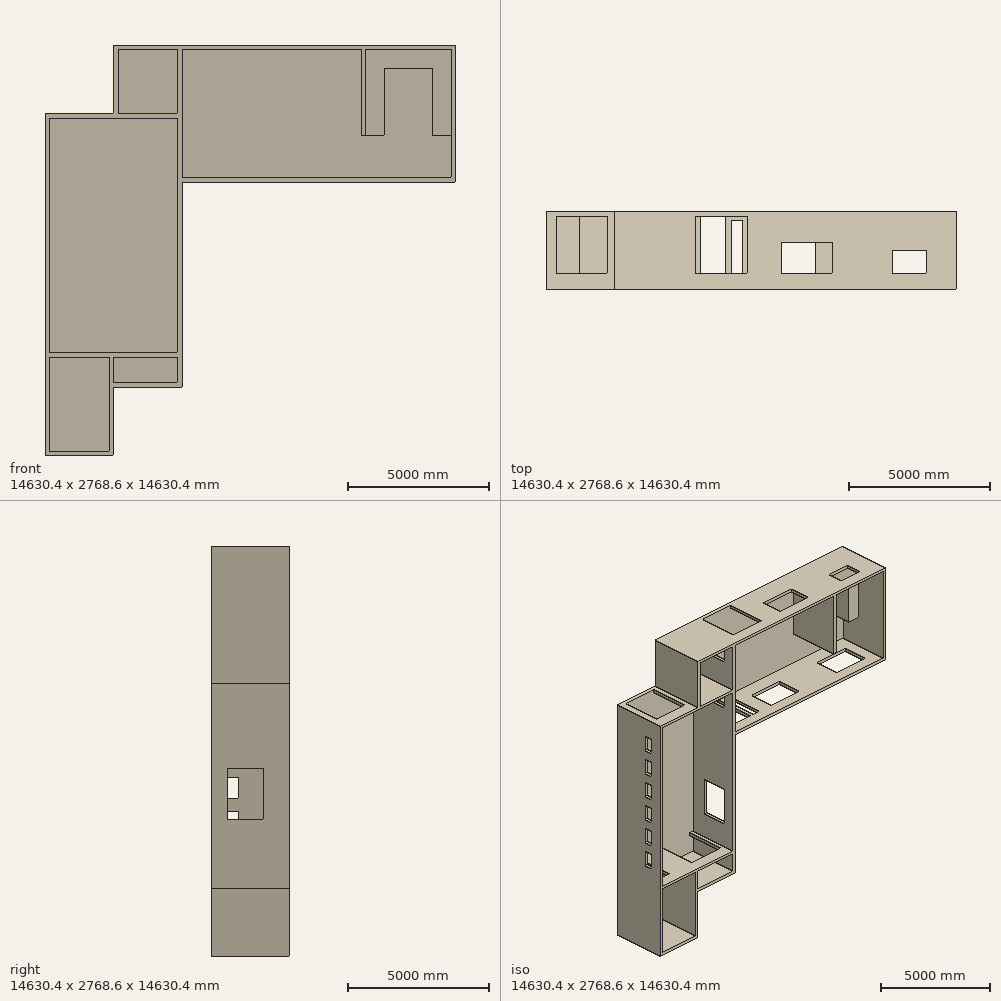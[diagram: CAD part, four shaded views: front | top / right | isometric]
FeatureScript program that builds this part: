
annotation { "Feature Type Name" : "Feature", "Feature Type Description" : "" }
export const myFeature = defineFeature(function(context is Context, id is Id, definition is map)
    precondition{}
    {
        {
            var Q0;
            Q0=qCreatedBy(makeId("Front.planeOp"),FACE);
            var sketch = newSketch(context, id + "F0", { "sketchPlane" : qUnion([Q0])});
            skLineSegment(sketch, "E0", {"start": v(0, 0) * mm, "end": v(0, 12192) * mm});
            skLineSegment(sketch, "E1", {"start": v(0, 12192) * mm, "end": v(2438.4, 12192) * mm});
            skLineSegment(sketch, "E2", {"start": v(2438.4, 12192) * mm, "end": v(2438.4, 14630.4) * mm});
            skLineSegment(sketch, "E3", {"start": v(2438.4, 14630.4) * mm, "end": v(14630.4, 14630.4) * mm});
            skLineSegment(sketch, "E4", {"start": v(14630.4, 14630.4) * mm, "end": v(14630.4, 9753.6) * mm});
            skLineSegment(sketch, "E5", {"start": v(14630.4, 9753.6) * mm, "end": v(4876.8, 9753.6) * mm});
            skLineSegment(sketch, "E6", {"start": v(4876.8, 9753.6) * mm, "end": v(4876.8, 2438.4) * mm});
            skLineSegment(sketch, "E7", {"start": v(4876.8, 2438.4) * mm, "end": v(2438.4, 2438.4) * mm});
            skLineSegment(sketch, "E8", {"start": v(2438.4, 2438.4) * mm, "end": v(2438.4, 0) * mm});
            skLineSegment(sketch, "E9", {"start": v(2438.4, 0) * mm, "end": v(0, 0) * mm});
            skLineSegment(sketch, "E10.0", {"start": v(2286, 152.4) * mm, "end": v(152.4, 152.4) * mm, "construction": true});
            skLineSegment(sketch, "E10.1", {"start": v(2286, 2590.8) * mm, "end": v(2286, 152.4) * mm, "construction": true});
            skLineSegment(sketch, "E10.2", {"start": v(152.4, 152.4) * mm, "end": v(152.4, 12039.6) * mm, "construction": true});
            skLineSegment(sketch, "E10.3", {"start": v(4724.4, 2590.8) * mm, "end": v(2286, 2590.8) * mm, "construction": true});
            skLineSegment(sketch, "E10.4", {"start": v(4724.4, 9906) * mm, "end": v(4724.4, 2590.8) * mm, "construction": true});
            skLineSegment(sketch, "E10.5", {"start": v(14478, 9906) * mm, "end": v(4724.4, 9906) * mm, "construction": true});
            skLineSegment(sketch, "E10.6", {"start": v(152.4, 12039.6) * mm, "end": v(2590.8, 12039.6) * mm, "construction": true});
            skLineSegment(sketch, "E10.7", {"start": v(2590.8, 12039.6) * mm, "end": v(2590.8, 14478) * mm, "construction": true});
            skLineSegment(sketch, "E10.8", {"start": v(2590.8, 14478) * mm, "end": v(14478, 14478) * mm, "construction": true});
            skLineSegment(sketch, "E10.9", {"start": v(14478, 14478) * mm, "end": v(14478, 9906) * mm, "construction": true});
            skSolve(sketch);
        }
        {
            var Q0;
            Q0 = qSketchRegion(id + "F0", true);
            extrude(context, id + "F1", {"entities" : qUnion([Q0]), "oppositeDirection" : true, "depth" : 177.8 * mm, "offsetDistance" : 25.4 * mm});
        }
        {
            var Q0;
            Q0=makeQuery(id+"F0.imprint","IMPRINT",FACE,{"disambiguationData":[TD([[makeQuery(id+"F0.imprint","IMPRINT",EDGE,{"derivedFrom":sQuery(id+"F0.wireOp",EDGE,"E0")}),-1.0]])]});
            var sketch = newSketch(context, id + "F2", { "sketchPlane" : qUnion([Q0])});
            skLineSegment(sketch, "E11.0", {"start": v(0, 0) * mm, "end": v(0, 12192) * mm});
            skLineSegment(sketch, "E12.0", {"start": v(0, 12192) * mm, "end": v(2438.4, 12192) * mm});
            skPoint(sketch, "E13.0", {"position": v(2438.4, 13411.2) * mm});
            skLineSegment(sketch, "E14.0", {"start": v(2438.4, 12192) * mm, "end": v(2438.4, 14630.4) * mm});
            skLineSegment(sketch, "E15.0", {"start": v(2438.4, 14630.4) * mm, "end": v(14630.4, 14630.4) * mm});
            skLineSegment(sketch, "E16.0", {"start": v(14630.4, 14630.4) * mm, "end": v(14630.4, 9753.6) * mm});
            skLineSegment(sketch, "E17.0", {"start": v(14630.4, 9753.6) * mm, "end": v(4876.8, 9753.6) * mm});
            skLineSegment(sketch, "E18.0", {"start": v(4876.8, 9753.6) * mm, "end": v(4876.8, 2438.4) * mm});
            skLineSegment(sketch, "E19.0", {"start": v(4876.8, 2438.4) * mm, "end": v(2438.4, 2438.4) * mm});
            skLineSegment(sketch, "E20.0", {"start": v(2438.4, 2438.4) * mm, "end": v(2438.4, 0) * mm});
            skLineSegment(sketch, "E21.0", {"start": v(2438.4, 0) * mm, "end": v(0, 0) * mm});
            skLineSegment(sketch, "E22.0", {"start": v(2286, 152.4) * mm, "end": v(152.4, 152.4) * mm});
            skLineSegment(sketch, "E23.0", {"start": v(2286, 2590.8) * mm, "end": v(2286, 152.4) * mm});
            skLineSegment(sketch, "E24.0", {"start": v(4724.4, 2590.8) * mm, "end": v(2286, 2590.8) * mm});
            skLineSegment(sketch, "E25.0", {"start": v(4724.4, 9906) * mm, "end": v(4724.4, 2590.8) * mm});
            skLineSegment(sketch, "E26.0", {"start": v(14478, 9906) * mm, "end": v(4724.4, 9906) * mm});
            skLineSegment(sketch, "E27.0", {"start": v(14478, 14478) * mm, "end": v(14478, 9906) * mm});
            skLineSegment(sketch, "E28.0", {"start": v(2590.8, 14478) * mm, "end": v(14478, 14478) * mm});
            skLineSegment(sketch, "E29.0", {"start": v(2590.8, 12039.6) * mm, "end": v(2590.8, 14478) * mm});
            skLineSegment(sketch, "E30.0", {"start": v(152.4, 12039.6) * mm, "end": v(2590.8, 12039.6) * mm});
            skLineSegment(sketch, "E31.0", {"start": v(152.4, 152.4) * mm, "end": v(152.4, 12039.6) * mm});
            skSolve(sketch);
        }
        {
            var Q0;
            Q0 = qSketchRegion(id + "F2", true);
            extrude(context, id + "F3", {"entities" : qUnion([Q0]), "operationType" : NewBodyOperationType.ADD, "depth" : 2590.8 * mm, "offsetDistance" : 25.4 * mm});
        }
        {
            var Q0;
            Q0=makeQuery(id+"F1.opExtrude","CAP_FACE",FACE,{"disambiguationData":[OSD([sQuery(id+"F0.wireOp",EDGE,"E0"),sQuery(id+"F0.wireOp",EDGE,"E1"),sQuery(id+"F0.wireOp",EDGE,"E2"),sQuery(id+"F0.wireOp",EDGE,"E3"),sQuery(id+"F0.wireOp",EDGE,"E4"),sQuery(id+"F0.wireOp",EDGE,"E5"),sQuery(id+"F0.wireOp",EDGE,"E6"),sQuery(id+"F0.wireOp",EDGE,"E7"),sQuery(id+"F0.wireOp",EDGE,"E8"),sQuery(id+"F0.wireOp",EDGE,"E9")])],"isStart":false});
            var sketch = newSketch(context, id + "F4", { "sketchPlane" : qUnion([Q0])});
            skLineSegment(sketch, "E32.0", {"start": v(-2235.2, 2641.6) * mm, "end": v(-2235.2, 203.2) * mm, "construction": true});
            skLineSegment(sketch, "E32.1", {"start": v(-4673.6, 2641.6) * mm, "end": v(-2235.2, 2641.6) * mm, "construction": true});
            skLineSegment(sketch, "E32.2", {"start": v(-2235.2, 203.2) * mm, "end": v(-203.2, 203.2) * mm, "construction": true});
            skLineSegment(sketch, "E32.3", {"start": v(-4673.6, 9956.8) * mm, "end": v(-4673.6, 2641.6) * mm, "construction": true});
            skLineSegment(sketch, "E32.4", {"start": v(-14427.2, 9956.8) * mm, "end": v(-4673.6, 9956.8) * mm, "construction": true});
            skLineSegment(sketch, "E32.5", {"start": v(-14427.2, 14427.2) * mm, "end": v(-14427.2, 9956.8) * mm, "construction": true});
            skLineSegment(sketch, "E32.6", {"start": v(-203.2, 203.2) * mm, "end": v(-203.2, 11988.8) * mm, "construction": true});
            skLineSegment(sketch, "E32.7", {"start": v(-203.2, 11988.8) * mm, "end": v(-2641.6, 11988.8) * mm, "construction": true});
            skLineSegment(sketch, "E32.8", {"start": v(-2641.6, 11988.8) * mm, "end": v(-2641.6, 14427.2) * mm, "construction": true});
            skLineSegment(sketch, "E32.9", {"start": v(-2641.6, 14427.2) * mm, "end": v(-14427.2, 14427.2) * mm, "construction": true});
            skCircle(sketch, "E33", {"center": v(-14427.2, 14427.2) * mm, "radius": 203.2 * mm});
            skCircle(sketch, "E34", {"center": v(-14427.2, 9956.8) * mm, "radius": 203.2 * mm});
            skCircle(sketch, "E35", {"center": v(-2641.6, 14427.2) * mm, "radius": 203.2 * mm});
            skCircle(sketch, "E36", {"center": v(-2641.6, 11988.8) * mm, "radius": 203.2 * mm});
            skCircle(sketch, "E37", {"center": v(-203.2, 11988.8) * mm, "radius": 203.2 * mm});
            skCircle(sketch, "E38", {"center": v(-203.2, 203.2) * mm, "radius": 203.2 * mm});
            skCircle(sketch, "E39", {"center": v(-2235.2, 203.2) * mm, "radius": 203.2 * mm});
            skCircle(sketch, "E40", {"center": v(-2235.2, 2641.6) * mm, "radius": 203.2 * mm});
            skCircle(sketch, "E41", {"center": v(-4673.6, 2641.6) * mm, "radius": 203.2 * mm});
            skCircle(sketch, "E42", {"center": v(-4673.6, 9956.8) * mm, "radius": 203.2 * mm});
            skLineSegment(sketch, "E43", {"start": v(-14427.2, 12192) * mm, "end": v(-2641.6, 12192) * mm, "construction": true});
            skCircle(sketch, "E44", {"center": v(-14427.2, 12192) * mm, "radius": 203.2 * mm});
            skCircle(sketch, "E45", {"center": v(-8534.4, 12192) * mm, "radius": 203.2 * mm});
            skCircle(sketch, "E46", {"center": v(-4673.6, 6299.2) * mm, "radius": 203.2 * mm});
            skCircle(sketch, "E47", {"center": v(-203.2, 6096) * mm, "radius": 203.2 * mm});
            skCircle(sketch, "E48", {"center": v(-9550.4, 9956.8) * mm, "radius": 203.2 * mm});
            skLineSegment(sketch, "E49", {"start": v(-2235.2, 2641.6) * mm, "end": v(-2235.2, 11988.8) * mm, "construction": true});
            skCircle(sketch, "E50", {"center": v(-2235.2, 7315.2) * mm, "radius": 203.2 * mm});
            skCircle(sketch, "E51", {"center": v(-8534.4, 14427.2) * mm, "radius": 203.2 * mm});
            skSolve(sketch);
        }
        {
            var Q0;
            Q0=makeQuery(id+"F1.opExtrude","CAP_FACE",FACE,{"disambiguationData":[OSD([sQuery(id+"F0.wireOp",EDGE,"E0"),sQuery(id+"F0.wireOp",EDGE,"E1"),sQuery(id+"F0.wireOp",EDGE,"E2"),sQuery(id+"F0.wireOp",EDGE,"E3"),sQuery(id+"F0.wireOp",EDGE,"E4"),sQuery(id+"F0.wireOp",EDGE,"E5"),sQuery(id+"F0.wireOp",EDGE,"E6"),sQuery(id+"F0.wireOp",EDGE,"E7"),sQuery(id+"F0.wireOp",EDGE,"E8"),sQuery(id+"F0.wireOp",EDGE,"E9")])],"isStart":true});
            var sketch = newSketch(context, id + "F5", { "sketchPlane" : qUnion([Q0])});
            skLineSegment(sketch, "E52", {"start": v(2590.8, 12039.6) * mm, "end": v(4724.4, 12039.6) * mm});
            skLineSegment(sketch, "E53", {"start": v(4724.4, 12039.6) * mm, "end": v(4724.4, 9906) * mm});
            skLineSegment(sketch, "E54.0", {"start": v(4876.8, 12192) * mm, "end": v(4876.8, 9906) * mm});
            skLineSegment(sketch, "E54.1", {"start": v(2590.8, 12192) * mm, "end": v(4876.8, 12192) * mm});
            skSolve(sketch);
        }
        {
            var Q0;
            Q0 = qSketchRegion(id + "F5", true);
            var Q1;
            {var subQ4=sQuery(id+"F5.wireOp",EDGE,"E52");Q1=makeQuery(id+"F5.imprint","IMPRINT",FACE,{"disambiguationData":[TD([[makeQuery(id+"F5.imprint","IMPRINT",EDGE,{"derivedFrom":subQ4}),1.0]])]});}
            extrude(context, id + "F6", {"entities" : qUnion([Q0, Q1]), "operationType" : NewBodyOperationType.ADD, "depth" : 2590.8 * mm, "offsetDistance" : 25.4 * mm});
        }
        {
            var Q0;
            Q0=makeQuery(id+"F3.boolean.opBoolean","MERGE",FACE,{"derivedFrom":[makeQuery(id+"F1.opExtrude","SWEPT_FACE",FACE,{"disambiguationData":[OSD([sQuery(id+"F0.wireOp",EDGE,"E5")])]}),makeQuery(id+"F3.opExtrude","SWEPT_FACE",FACE,{"disambiguationData":[OSD([sQuery(id+"F2.wireOp",EDGE,"E17.0")])]})]});
            var sketch = newSketch(context, id + "F7", { "sketchPlane" : qUnion([Q0])});
            skLineSegment(sketch, "E55.bottom", {"start": v(5486.4, 0) * mm, "end": v(6400.8, 0) * mm});
            skLineSegment(sketch, "E55.top", {"start": v(5486.4, 2032) * mm, "end": v(6400.8, 2032) * mm});
            skLineSegment(sketch, "E55.left", {"start": v(5486.4, 0) * mm, "end": v(5486.4, 2032) * mm});
            skLineSegment(sketch, "E55.right", {"start": v(6400.8, 0) * mm, "end": v(6400.8, 2032) * mm});
            skLineSegment(sketch, "E56.bottom", {"start": v(6604, 2032) * mm, "end": v(7010.4, 2032) * mm});
            skLineSegment(sketch, "E56.top", {"start": v(6604, 152.4) * mm, "end": v(7010.4, 152.4) * mm});
            skLineSegment(sketch, "E56.left", {"start": v(6604, 2032) * mm, "end": v(6604, 152.4) * mm});
            skLineSegment(sketch, "E56.right", {"start": v(7010.4, 2032) * mm, "end": v(7010.4, 152.4) * mm});
            skLineSegment(sketch, "E57.bottom", {"start": v(7772.4, 2032) * mm, "end": v(9601.2, 2032) * mm});
            skLineSegment(sketch, "E57.top", {"start": v(7772.4, 736.6) * mm, "end": v(9601.2, 736.6) * mm});
            skLineSegment(sketch, "E57.left", {"start": v(7772.4, 2032) * mm, "end": v(7772.4, 736.6) * mm});
            skLineSegment(sketch, "E57.right", {"start": v(9601.2, 2032) * mm, "end": v(9601.2, 736.6) * mm});
            skLineSegment(sketch, "E58.bottom", {"start": v(12039.6, 2032) * mm, "end": v(13868.4, 2032) * mm});
            skLineSegment(sketch, "E58.top", {"start": v(12039.6, 736.6) * mm, "end": v(13868.4, 736.6) * mm});
            skLineSegment(sketch, "E58.left", {"start": v(12039.6, 2032) * mm, "end": v(12039.6, 736.6) * mm});
            skLineSegment(sketch, "E58.right", {"start": v(13868.4, 2032) * mm, "end": v(13868.4, 736.6) * mm});
            skSolve(sketch);
        }
        {
            var Q0;
            Q0 = qSketchRegion(id + "F7", true);
            extrude(context, id + "F8", {"entities" : qUnion([Q0]), "operationType" : NewBodyOperationType.REMOVE, "endBound" : BoundingType.UP_TO_NEXT, "oppositeDirection" : true, "depth" : 25.4 * mm, "offsetDistance" : 25.4 * mm});
        }
        {
            var Q0;
            Q0=makeQuery(id+"F8.boolean.opBoolean","MERGE",FACE,{"derivedFrom":[makeQuery(id+"F6.boolean.opBoolean","SPLIT",FACE,{"disambiguationData":[TD([makeQuery(id+"F3.opExtrude","SWEPT_FACE",FACE,{"disambiguationData":[OSD([sQuery(id+"F2.wireOp",EDGE,"E26.0")])]})])],"derivedFrom":makeQuery(id+"F1.opExtrude","CAP_FACE",FACE,{"disambiguationData":[OSD([sQuery(id+"F0.wireOp",EDGE,"E0"),sQuery(id+"F0.wireOp",EDGE,"E1"),sQuery(id+"F0.wireOp",EDGE,"E2"),sQuery(id+"F0.wireOp",EDGE,"E3"),sQuery(id+"F0.wireOp",EDGE,"E4"),sQuery(id+"F0.wireOp",EDGE,"E5"),sQuery(id+"F0.wireOp",EDGE,"E6"),sQuery(id+"F0.wireOp",EDGE,"E7"),sQuery(id+"F0.wireOp",EDGE,"E8"),sQuery(id+"F0.wireOp",EDGE,"E9")])],"isStart":true})}),makeQuery(id+"F8.opExtrude","SWEPT_FACE",FACE,{"disambiguationData":[OSD([sQuery(id+"F7.wireOp",EDGE,"E55.bottom")])]})]});
            var sketch = newSketch(context, id + "F9", { "sketchPlane" : qUnion([Q0])});
            skLineSegment(sketch, "E59.bottom", {"start": v(11277.6, 14478) * mm, "end": v(11430, 14478) * mm});
            skLineSegment(sketch, "E59.top", {"start": v(11277.6, 11430) * mm, "end": v(11430, 11430) * mm});
            skLineSegment(sketch, "E59.left", {"start": v(11277.6, 14478) * mm, "end": v(11277.6, 11430) * mm});
            skLineSegment(sketch, "E59.right", {"start": v(11430, 14478) * mm, "end": v(11430, 11430) * mm});
            skSolve(sketch);
        }
        {
            var Q0;
            Q0 = qSketchRegion(id + "F9", true);
            extrude(context, id + "F10", {"entities" : qUnion([Q0]), "operationType" : NewBodyOperationType.ADD, "depth" : 2590.8 * mm, "offsetDistance" : 25.4 * mm});
        }
        {
            var Q0;
            Q0=makeQuery(id+"F6.boolean.opBoolean","SPLIT",FACE,{"disambiguationData":[TD([makeQuery(id+"F3.opExtrude","SWEPT_FACE",FACE,{"disambiguationData":[OSD([sQuery(id+"F2.wireOp",EDGE,"E22.0")])]})])],"derivedFrom":makeQuery(id+"F1.opExtrude","CAP_FACE",FACE,{"disambiguationData":[OSD([sQuery(id+"F0.wireOp",EDGE,"E0"),sQuery(id+"F0.wireOp",EDGE,"E1"),sQuery(id+"F0.wireOp",EDGE,"E2"),sQuery(id+"F0.wireOp",EDGE,"E3"),sQuery(id+"F0.wireOp",EDGE,"E4"),sQuery(id+"F0.wireOp",EDGE,"E5"),sQuery(id+"F0.wireOp",EDGE,"E6"),sQuery(id+"F0.wireOp",EDGE,"E7"),sQuery(id+"F0.wireOp",EDGE,"E8"),sQuery(id+"F0.wireOp",EDGE,"E9")])],"isStart":true})});
            var sketch = newSketch(context, id + "F11", { "sketchPlane" : qUnion([Q0])});
            skLineSegment(sketch, "E60", {"start": v(152.4, 3657.6) * mm, "end": v(4724.4, 3657.6) * mm});
            skLineSegment(sketch, "E61", {"start": v(152.4, 3505.2) * mm, "end": v(2286, 3505.2) * mm});
            skLineSegment(sketch, "E62", {"start": v(2286, 3505.2) * mm, "end": v(2286, 2590.8) * mm});
            skLineSegment(sketch, "E63", {"start": v(2438.4, 2590.8) * mm, "end": v(2438.4, 3505.2) * mm});
            skLineSegment(sketch, "E64", {"start": v(2438.4, 3505.2) * mm, "end": v(4724.4, 3505.2) * mm});
            skSolve(sketch);
        }
        {
            var Q0;
            Q0 = qSketchRegion(id + "F11", true);
            var Q1;
            {var subQ3=sQuery(id+"F11.wireOp",EDGE,"E60");Q1=makeQuery(id+"F11.imprint","IMPRINT",FACE,{"disambiguationData":[TD([[makeQuery(id+"F11.imprint","IMPRINT",EDGE,{"derivedFrom":subQ3}),-1.0]])]});}
            extrude(context, id + "F12", {"entities" : qUnion([Q0, Q1]), "operationType" : NewBodyOperationType.ADD, "depth" : 2590.8 * mm, "offsetDistance" : 25.4 * mm});
        }
        {
            var Q0;
            Q0=makeQuery(id+"F12.opExtrude","SWEPT_FACE",FACE,{"disambiguationData":[OSD([sQuery(id+"F11.wireOp",EDGE,"E60")])]});
            var sketch = newSketch(context, id + "F13", { "sketchPlane" : qUnion([Q0])});
            skLineSegment(sketch, "E65.bottom", {"start": v(355.6, 0) * mm, "end": v(1168.4, 0) * mm});
            skLineSegment(sketch, "E65.top", {"start": v(355.6, -2032) * mm, "end": v(1168.4, -2032) * mm});
            skLineSegment(sketch, "E65.left", {"start": v(355.6, 0) * mm, "end": v(355.6, -2032) * mm});
            skLineSegment(sketch, "E65.right", {"start": v(1168.4, 0) * mm, "end": v(1168.4, -2032) * mm});
            skLineSegment(sketch, "E66.bottom", {"start": v(4521.2, 0) * mm, "end": v(2641.6, 0) * mm});
            skLineSegment(sketch, "E66.top", {"start": v(4521.2, -2032) * mm, "end": v(2641.6, -2032) * mm});
            skLineSegment(sketch, "E66.left", {"start": v(4521.2, 0) * mm, "end": v(4521.2, -2032) * mm});
            skLineSegment(sketch, "E66.right", {"start": v(2641.6, 0) * mm, "end": v(2641.6, -2032) * mm});
            skSolve(sketch);
        }
        {
            var Q0;
            Q0 = qSketchRegion(id + "F13", true);
            extrude(context, id + "F14", {"entities" : qUnion([Q0]), "operationType" : NewBodyOperationType.REMOVE, "endBound" : BoundingType.UP_TO_NEXT, "oppositeDirection" : true, "depth" : 25.4 * mm, "offsetDistance" : 25.4 * mm});
        }
        {
            var Q0;
            Q0=makeQuery(id+"F8.boolean.opBoolean","MERGE",FACE,{"derivedFrom":[makeQuery(id+"F6.boolean.opBoolean","SPLIT",FACE,{"disambiguationData":[TD([makeQuery(id+"F3.opExtrude","SWEPT_FACE",FACE,{"disambiguationData":[OSD([sQuery(id+"F2.wireOp",EDGE,"E26.0")])]})])],"derivedFrom":makeQuery(id+"F1.opExtrude","CAP_FACE",FACE,{"disambiguationData":[OSD([sQuery(id+"F0.wireOp",EDGE,"E0"),sQuery(id+"F0.wireOp",EDGE,"E1"),sQuery(id+"F0.wireOp",EDGE,"E2"),sQuery(id+"F0.wireOp",EDGE,"E3"),sQuery(id+"F0.wireOp",EDGE,"E4"),sQuery(id+"F0.wireOp",EDGE,"E5"),sQuery(id+"F0.wireOp",EDGE,"E6"),sQuery(id+"F0.wireOp",EDGE,"E7"),sQuery(id+"F0.wireOp",EDGE,"E8"),sQuery(id+"F0.wireOp",EDGE,"E9")])],"isStart":true})}),makeQuery(id+"F8.opExtrude","SWEPT_FACE",FACE,{"disambiguationData":[OSD([sQuery(id+"F7.wireOp",EDGE,"E55.bottom")])]})]});
            var sketch = newSketch(context, id + "F15", { "sketchPlane" : qUnion([Q0])});
            skLineSegment(sketch, "E67", {"start": v(4876.8, 12192) * mm, "end": v(4876.8, 14478) * mm});
            skLineSegment(sketch, "E68", {"start": v(4724.4, 14478) * mm, "end": v(4724.4, 12192) * mm});
            skSolve(sketch);
        }
        {
            var Q0;
            Q0 = qSketchRegion(id + "F15", true);
            var Q1;
            {var subQ0=sQuery(id+"F15.wireOp",EDGE,"E67");Q1=makeQuery(id+"F15.imprint","IMPRINT",FACE,{"disambiguationData":[TD([[makeQuery(id+"F15.imprint","IMPRINT",EDGE,{"derivedFrom":subQ0}),1.0]])]});}
            extrude(context, id + "F16", {"entities" : qUnion([Q0, Q1]), "operationType" : NewBodyOperationType.ADD, "depth" : 2590.8 * mm, "offsetDistance" : 25.4 * mm});
        }
        {
            var Q0;
            Q0=makeQuery(id+"F16.boolean.opBoolean","MERGE",FACE,{"derivedFrom":[makeQuery(id+"F6.opExtrude","SWEPT_FACE",FACE,{"disambiguationData":[OSD([sQuery(id+"F5.wireOp",EDGE,"E54.0")])]}),makeQuery(id+"F16.opExtrude","SWEPT_FACE",FACE,{"disambiguationData":[OSD([sQuery(id+"F15.wireOp",EDGE,"E67")])]})]});
            var sketch = newSketch(context, id + "F17", { "sketchPlane" : qUnion([Q0])});
            skLineSegment(sketch, "E69.bottom", {"start": v(0, 14274.8) * mm, "end": v(-2032, 14274.8) * mm});
            skLineSegment(sketch, "E69.top", {"start": v(0, 13462) * mm, "end": v(-2032, 13462) * mm});
            skLineSegment(sketch, "E69.left", {"start": v(0, 14274.8) * mm, "end": v(0, 13462) * mm});
            skLineSegment(sketch, "E69.right", {"start": v(-2032, 14274.8) * mm, "end": v(-2032, 13462) * mm});
            skSolve(sketch);
        }
        {
            var Q0;
            Q0 = qSketchRegion(id + "F17", true);
            extrude(context, id + "F18", {"entities" : qUnion([Q0]), "operationType" : NewBodyOperationType.REMOVE, "endBound" : BoundingType.UP_TO_NEXT, "oppositeDirection" : true, "depth" : 25.4 * mm, "offsetDistance" : 25.4 * mm});
        }
        {
            var Q0;
            Q0=makeQuery(id+"F16.boolean.opBoolean","MERGE",FACE,{"derivedFrom":[makeQuery(id+"F6.opExtrude","SWEPT_FACE",FACE,{"disambiguationData":[OSD([sQuery(id+"F5.wireOp",EDGE,"E54.0")])]}),makeQuery(id+"F16.opExtrude","SWEPT_FACE",FACE,{"disambiguationData":[OSD([sQuery(id+"F15.wireOp",EDGE,"E67")])]})]});
            var sketch = newSketch(context, id + "F19", { "sketchPlane" : qUnion([Q0])});
            skLineSegment(sketch, "E70.bottom", {"start": v(0, 11836.4) * mm, "end": v(-2032, 11836.4) * mm});
            skLineSegment(sketch, "E70.top", {"start": v(0, 11023.6) * mm, "end": v(-2032, 11023.6) * mm});
            skLineSegment(sketch, "E70.left", {"start": v(0, 11836.4) * mm, "end": v(0, 11023.6) * mm});
            skLineSegment(sketch, "E70.right", {"start": v(-2032, 11836.4) * mm, "end": v(-2032, 11023.6) * mm});
            skSolve(sketch);
        }
        {
            var Q0;
            Q0 = qSketchRegion(id + "F19", true);
            extrude(context, id + "F20", {"entities" : qUnion([Q0]), "operationType" : NewBodyOperationType.REMOVE, "endBound" : BoundingType.UP_TO_NEXT, "oppositeDirection" : true, "depth" : 25.4 * mm, "offsetDistance" : 25.4 * mm});
        }
        {
            var Q0;
            {var subQ1=sQuery(id+"F5.wireOp",EDGE,"E54.0");var subQ3=sQuery(id+"F2.wireOp",EDGE,"E29.0");var subQ8=sQuery(id+"F2.wireOp",EDGE,"E28.0");Q0=makeQuery(id+"F16.boolean.opBoolean","SPLIT",FACE,{"disambiguationData":[TD([makeQuery(id+"F6.opExtrude","SWEPT_FACE",FACE,{"disambiguationData":[OSD([subQ1])]})])],"derivedFrom":makeQuery(id+"F10.boolean.opBoolean","SPLIT",FACE,{"disambiguationData":[TD([makeQuery(id+"F3.opExtrude","SWEPT_FACE",FACE,{"disambiguationData":[OSD([subQ3])]})])],"derivedFrom":makeQuery(id+"F3.opExtrude","SWEPT_FACE",FACE,{"disambiguationData":[OSD([subQ8])]})})});}
            var sketch = newSketch(context, id + "F21", { "sketchPlane" : qUnion([Q0])});
            skLineSegment(sketch, "E71.bottom", {"start": v(5334, 0) * mm, "end": v(7162.8, 0) * mm});
            skLineSegment(sketch, "E71.top", {"start": v(5334, 2032) * mm, "end": v(7162.8, 2032) * mm});
            skLineSegment(sketch, "E71.left", {"start": v(5334, 0) * mm, "end": v(5334, 2032) * mm});
            skLineSegment(sketch, "E71.right", {"start": v(7162.8, 0) * mm, "end": v(7162.8, 2032) * mm});
            skLineSegment(sketch, "E72.bottom", {"start": v(8382, 2032) * mm, "end": v(10210.8, 2032) * mm});
            skLineSegment(sketch, "E72.top", {"start": v(8382, 914.4) * mm, "end": v(10210.8, 914.4) * mm});
            skLineSegment(sketch, "E72.left", {"start": v(8382, 2032) * mm, "end": v(8382, 914.4) * mm});
            skLineSegment(sketch, "E72.right", {"start": v(10210.8, 2032) * mm, "end": v(10210.8, 914.4) * mm});
            skLineSegment(sketch, "E73.bottom", {"start": v(12344.4, 2032) * mm, "end": v(13563.6, 2032) * mm});
            skLineSegment(sketch, "E73.top", {"start": v(12344.4, 1219.2) * mm, "end": v(13563.6, 1219.2) * mm});
            skLineSegment(sketch, "E73.left", {"start": v(12344.4, 2032) * mm, "end": v(12344.4, 1219.2) * mm});
            skLineSegment(sketch, "E73.right", {"start": v(13563.6, 2032) * mm, "end": v(13563.6, 1219.2) * mm});
            skSolve(sketch);
        }
        {
            var Q0;
            Q0 = qSketchRegion(id + "F21", true);
            extrude(context, id + "F22", {"entities" : qUnion([Q0]), "operationType" : NewBodyOperationType.REMOVE, "endBound" : BoundingType.UP_TO_NEXT, "oppositeDirection" : true, "depth" : 25.4 * mm, "offsetDistance" : 25.4 * mm});
        }
        {
            var Q0;
            {var subQ2=makeQuery(id+"F3.opExtrude","SWEPT_FACE",FACE,{"disambiguationData":[OSD([sQuery(id+"F2.wireOp",EDGE,"E29.0")])]});var subQ4=makeQuery(id+"F3.opExtrude","SWEPT_FACE",FACE,{"disambiguationData":[OSD([sQuery(id+"F2.wireOp",EDGE,"E26.0")])]});var subQ6=sQuery(id+"F0.wireOp",EDGE,"E5");var subQ7=makeQuery(id+"F1.opExtrude","CAP_FACE",FACE,{"disambiguationData":[OSD([sQuery(id+"F0.wireOp",EDGE,"E0"),sQuery(id+"F0.wireOp",EDGE,"E1"),sQuery(id+"F0.wireOp",EDGE,"E2"),sQuery(id+"F0.wireOp",EDGE,"E3"),sQuery(id+"F0.wireOp",EDGE,"E4"),subQ6,sQuery(id+"F0.wireOp",EDGE,"E6"),sQuery(id+"F0.wireOp",EDGE,"E7"),sQuery(id+"F0.wireOp",EDGE,"E8"),sQuery(id+"F0.wireOp",EDGE,"E9")])],"isStart":true});var subQ8=makeQuery(id+"F8.boolean.opBoolean","MERGE",FACE,{"derivedFrom":[makeQuery(id+"F6.boolean.opBoolean","SPLIT",FACE,{"disambiguationData":[TD([subQ4])],"derivedFrom":subQ7}),makeQuery(id+"F8.opExtrude","SWEPT_FACE",FACE,{"disambiguationData":[OSD([sQuery(id+"F7.wireOp",EDGE,"E55.bottom")])]})]});var subQ11=makeQuery(id+"F3.opExtrude","SWEPT_FACE",FACE,{"disambiguationData":[OSD([sQuery(id+"F2.wireOp",EDGE,"E30.0")])]});var subQ14=makeQuery(id+"F3.opExtrude","SWEPT_FACE",FACE,{"disambiguationData":[OSD([sQuery(id+"F2.wireOp",EDGE,"E24.0")])]});var subQ16=makeQuery(id+"F3.opExtrude","SWEPT_FACE",FACE,{"disambiguationData":[OSD([sQuery(id+"F2.wireOp",EDGE,"E22.0")])]});var subQ17=makeQuery(id+"F6.boolean.opBoolean","SPLIT",FACE,{"disambiguationData":[TD([subQ16])],"derivedFrom":subQ7});Q0=makeQuery(id+"F22.boolean.opBoolean","MERGE",FACE,{"derivedFrom":[makeQuery(id+"F20.boolean.opBoolean","MERGE",FACE,{"derivedFrom":[makeQuery(id+"F14.boolean.opBoolean","MERGE",FACE,{"derivedFrom":[makeQuery(id+"F12.boolean.opBoolean","SPLIT",FACE,{"disambiguationData":[TD([subQ16])],"derivedFrom":subQ17}),makeQuery(id+"F12.boolean.opBoolean","SPLIT",FACE,{"disambiguationData":[TD([subQ14])],"derivedFrom":subQ17}),makeQuery(id+"F12.boolean.opBoolean","SPLIT",FACE,{"disambiguationData":[TD([subQ11])],"derivedFrom":subQ17}),makeQuery(id+"F14.opExtrude","SWEPT_FACE",FACE,{"disambiguationData":[OSD([sQuery(id+"F13.wireOp",EDGE,"E65.bottom")])]}),makeQuery(id+"F14.opExtrude","SWEPT_FACE",FACE,{"disambiguationData":[OSD([sQuery(id+"F13.wireOp",EDGE,"E66.bottom")])]})]}),makeQuery(id+"F18.boolean.opBoolean","MERGE",FACE,{"derivedFrom":[makeQuery(id+"F16.boolean.opBoolean","SPLIT",FACE,{"disambiguationData":[TD([makeQuery(id+"F1.opExtrude","SWEPT_FACE",FACE,{"disambiguationData":[OSD([subQ6])]})])],"derivedFrom":subQ8}),makeQuery(id+"F16.boolean.opBoolean","SPLIT",FACE,{"disambiguationData":[TD([subQ2])],"derivedFrom":subQ8}),makeQuery(id+"F18.opExtrude","SWEPT_FACE",FACE,{"disambiguationData":[OSD([sQuery(id+"F17.wireOp",EDGE,"E69.left")])]})]}),makeQuery(id+"F20.opExtrude","SWEPT_FACE",FACE,{"disambiguationData":[OSD([sQuery(id+"F19.wireOp",EDGE,"E70.left")])]})]}),makeQuery(id+"F22.opExtrude","SWEPT_FACE",FACE,{"disambiguationData":[OSD([sQuery(id+"F21.wireOp",EDGE,"E71.bottom")])]})]});}
            var sketch = newSketch(context, id + "F23", { "sketchPlane" : qUnion([Q0])});
            skLineSegment(sketch, "E74", {"start": v(11430, 11430) * mm, "end": v(12090.4, 11430) * mm});
            skLineSegment(sketch, "E75", {"start": v(12090.4, 11430) * mm, "end": v(12090.4, 13817.6) * mm});
            skLineSegment(sketch, "E76", {"start": v(12090.4, 13817.6) * mm, "end": v(13817.6, 13817.6) * mm});
            skLineSegment(sketch, "E77", {"start": v(13817.6, 13817.6) * mm, "end": v(13817.6, 11430) * mm});
            skLineSegment(sketch, "E78", {"start": v(13817.6, 11430) * mm, "end": v(14478, 11430) * mm});
            skSolve(sketch);
        }
        {
            var Q0;
            Q0 = qSketchRegion(id + "F23", true);
            var Q1;
            Q1=makeQuery(id+"F23.imprint","IMPRINT",FACE,{"disambiguationData":[TD([[makeQuery(id+"F23.imprint","IMPRINT",EDGE,{"derivedFrom":sQuery(id+"F23.wireOp",EDGE,"E74")}),1.0]])]});
            extrude(context, id + "F24", {"entities" : qUnion([Q0, Q1]), "operationType" : NewBodyOperationType.ADD, "depth" : 1016 * mm, "offsetDistance" : 25.4 * mm});
        }
        {
            var Q0;
            Q0=makeQuery(id+"F6.boolean.opBoolean","MERGE",FACE,{"derivedFrom":[makeQuery(id+"F3.opExtrude","SWEPT_FACE",FACE,{"disambiguationData":[OSD([sQuery(id+"F2.wireOp",EDGE,"E30.0")])]}),makeQuery(id+"F6.opExtrude","SWEPT_FACE",FACE,{"disambiguationData":[OSD([sQuery(id+"F5.wireOp",EDGE,"E52")])]})]});
            var sketch = newSketch(context, id + "F25", { "sketchPlane" : qUnion([Q0])});
            skLineSegment(sketch, "E79.bottom", {"start": v(355.6, 0) * mm, "end": v(2184.4, 0) * mm});
            skLineSegment(sketch, "E79.top", {"start": v(355.6, 2032) * mm, "end": v(2184.4, 2032) * mm});
            skLineSegment(sketch, "E79.left", {"start": v(355.6, 0) * mm, "end": v(355.6, 2032) * mm});
            skLineSegment(sketch, "E79.right", {"start": v(2184.4, 0) * mm, "end": v(2184.4, 2032) * mm});
            skSolve(sketch);
        }
        {
            var Q0;
            Q0 = qSketchRegion(id + "F25", true);
            extrude(context, id + "F26", {"entities" : qUnion([Q0]), "operationType" : NewBodyOperationType.REMOVE, "endBound" : BoundingType.UP_TO_NEXT, "oppositeDirection" : true, "depth" : 25.4 * mm, "offsetDistance" : 25.4 * mm});
        }
        {
            var Q0;
            {var subQ1=sQuery(id+"F2.wireOp",EDGE,"E30.0");var subQ5=sQuery(id+"F2.wireOp",EDGE,"E25.0");var subQ8=sQuery(id+"F5.wireOp",EDGE,"E53");Q0=makeQuery(id+"F12.boolean.opBoolean","SPLIT",FACE,{"disambiguationData":[TD([makeQuery(id+"F3.opExtrude","SWEPT_FACE",FACE,{"disambiguationData":[OSD([subQ1])]})])],"derivedFrom":makeQuery(id+"F6.boolean.opBoolean","MERGE",FACE,{"derivedFrom":[makeQuery(id+"F3.opExtrude","SWEPT_FACE",FACE,{"disambiguationData":[OSD([subQ5])]}),makeQuery(id+"F6.opExtrude","SWEPT_FACE",FACE,{"disambiguationData":[OSD([subQ8])]})]})});}
            var sketch = newSketch(context, id + "F27", { "sketchPlane" : qUnion([Q0])});
            skLineSegment(sketch, "E80.bottom", {"start": v(2032, 6705.6) * mm, "end": v(736.6, 6705.6) * mm});
            skLineSegment(sketch, "E80.top", {"start": v(2032, 4876.8) * mm, "end": v(736.6, 4876.8) * mm});
            skLineSegment(sketch, "E80.left", {"start": v(2032, 6705.6) * mm, "end": v(2032, 4876.8) * mm});
            skLineSegment(sketch, "E80.right", {"start": v(736.6, 6705.6) * mm, "end": v(736.6, 4876.8) * mm});
            skSolve(sketch);
        }
        {
            var Q0;
            Q0 = qSketchRegion(id + "F27", true);
            extrude(context, id + "F28", {"entities" : qUnion([Q0]), "operationType" : NewBodyOperationType.REMOVE, "endBound" : BoundingType.UP_TO_NEXT, "oppositeDirection" : true, "depth" : 25.4 * mm, "offsetDistance" : 25.4 * mm});
        }
        {
            var Q0;
            {var subQ1=sQuery(id+"F2.wireOp",EDGE,"E30.0");var subQ2=sQuery(id+"F2.wireOp",EDGE,"E31.0");Q0=makeQuery(id+"F12.boolean.opBoolean","SPLIT",FACE,{"disambiguationData":[TD([makeQuery(id+"F3.opExtrude","SWEPT_FACE",FACE,{"disambiguationData":[OSD([subQ1])]})])],"derivedFrom":makeQuery(id+"F3.opExtrude","SWEPT_FACE",FACE,{"disambiguationData":[OSD([subQ2])]})});}
            var sketch = newSketch(context, id + "F29", { "sketchPlane" : qUnion([Q0])});
            skLineSegment(sketch, "E81.bottom", {"start": v(-2032, 4419.6) * mm, "end": v(-1625.6, 4419.6) * mm});
            skLineSegment(sketch, "E81.top", {"start": v(-2032, 5181.6) * mm, "end": v(-1625.6, 5181.6) * mm});
            skLineSegment(sketch, "E81.left", {"start": v(-2032, 4419.6) * mm, "end": v(-2032, 5181.6) * mm});
            skLineSegment(sketch, "E81.right", {"start": v(-1625.6, 4419.6) * mm, "end": v(-1625.6, 5181.6) * mm});
            skLineSegment(sketch, "E82.0.1.0", {"start": v(-2032, 5638.8) * mm, "end": v(-2032, 6400.8) * mm});
            skLineSegment(sketch, "E82.0.1.1", {"start": v(-2032, 5638.8) * mm, "end": v(-1625.6, 5638.8) * mm});
            skLineSegment(sketch, "E82.0.1.2", {"start": v(-1625.6, 5638.8) * mm, "end": v(-1625.6, 6400.8) * mm});
            skLineSegment(sketch, "E82.0.1.3", {"start": v(-2032, 6400.8) * mm, "end": v(-1625.6, 6400.8) * mm});
            skLineSegment(sketch, "E82.0.2.0", {"start": v(-2032, 6858) * mm, "end": v(-2032, 7620) * mm});
            skLineSegment(sketch, "E82.0.2.1", {"start": v(-2032, 6858) * mm, "end": v(-1625.6, 6858) * mm});
            skLineSegment(sketch, "E82.0.2.2", {"start": v(-1625.6, 6858) * mm, "end": v(-1625.6, 7620) * mm});
            skLineSegment(sketch, "E82.0.2.3", {"start": v(-2032, 7620) * mm, "end": v(-1625.6, 7620) * mm});
            skLineSegment(sketch, "E82.0.3.0", {"start": v(-2032, 8077.2) * mm, "end": v(-2032, 8839.2) * mm});
            skLineSegment(sketch, "E82.0.3.1", {"start": v(-2032, 8077.2) * mm, "end": v(-1625.6, 8077.2) * mm});
            skLineSegment(sketch, "E82.0.3.2", {"start": v(-1625.6, 8077.2) * mm, "end": v(-1625.6, 8839.2) * mm});
            skLineSegment(sketch, "E82.0.3.3", {"start": v(-2032, 8839.2) * mm, "end": v(-1625.6, 8839.2) * mm});
            skLineSegment(sketch, "E82.0.4.0", {"start": v(-2032, 9296.4) * mm, "end": v(-2032, 10058.4) * mm});
            skLineSegment(sketch, "E82.0.4.1", {"start": v(-2032, 9296.4) * mm, "end": v(-1625.6, 9296.4) * mm});
            skLineSegment(sketch, "E82.0.4.2", {"start": v(-1625.6, 9296.4) * mm, "end": v(-1625.6, 10058.4) * mm});
            skLineSegment(sketch, "E82.0.4.3", {"start": v(-2032, 10058.4) * mm, "end": v(-1625.6, 10058.4) * mm});
            skLineSegment(sketch, "E82.0.5.0", {"start": v(-2032, 10515.6) * mm, "end": v(-2032, 11277.6) * mm});
            skLineSegment(sketch, "E82.0.5.1", {"start": v(-2032, 10515.6) * mm, "end": v(-1625.6, 10515.6) * mm});
            skLineSegment(sketch, "E82.0.5.2", {"start": v(-1625.6, 10515.6) * mm, "end": v(-1625.6, 11277.6) * mm});
            skLineSegment(sketch, "E82.0.5.3", {"start": v(-2032, 11277.6) * mm, "end": v(-1625.6, 11277.6) * mm});
            skLineSegment(sketch, "E82.direction1", {"start": v(-2032, 4419.6) * mm, "end": v(-1625.6, 4419.6) * mm, "construction": true});
            skLineSegment(sketch, "E82.direction2", {"start": v(-2032, 4419.6) * mm, "end": v(-2032, 5638.8) * mm, "construction": true});
            skSolve(sketch);
        }
        {
            var Q0;
            Q0 = qSketchRegion(id + "F29", true);
            extrude(context, id + "F30", {"entities" : qUnion([Q0]), "operationType" : NewBodyOperationType.REMOVE, "endBound" : BoundingType.UP_TO_NEXT, "oppositeDirection" : true, "depth" : 25.4 * mm, "offsetDistance" : 25.4 * mm});
        }
    });
